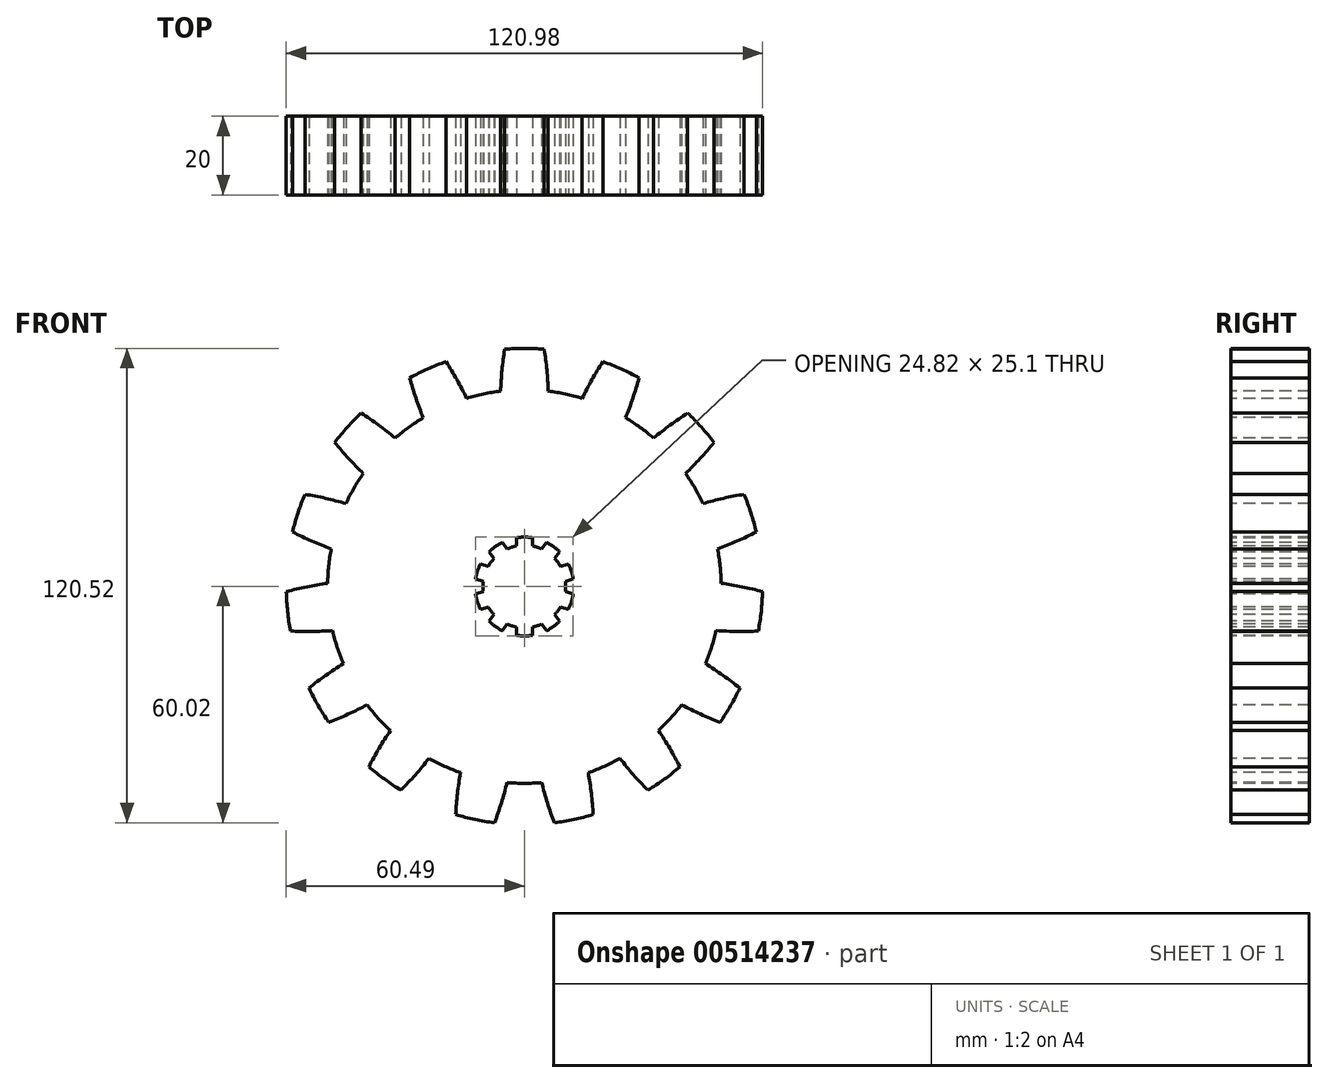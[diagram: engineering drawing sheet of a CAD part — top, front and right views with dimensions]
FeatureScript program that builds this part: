
annotation { "Feature Type Name" : "Feature", "Feature Type Description" : "" }
export const myFeature = defineFeature(function(context is Context, id is Id, definition is map)
    precondition{}
    {
        {
            var Q0;
            Q0=qCreatedBy(makeId("Front.planeOp"),FACE);
            var sketch = newSketch(context, id + "F0", { "sketchPlane" : qUnion([Q0])});
            skCircle(sketch, "E0", {"center": v(0, 0) * mm, "radius": 50 * mm});
            skArc(sketch, "E1", {"start": v(5.04, 60.29) * mm, "mid": v(0, 60.5) * mm, "end": v(-5.04, 60.29) * mm});
            skArc(sketch, "E2", {"start": v(-5.04, 60.29) * mm, "mid": v(-5.7, 54.98) * mm, "end": v(-6.05, 49.63) * mm});
            skArc(sketch, "E3.trimOffspring", {"start": v(6.05, 49.63) * mm, "mid": v(5.7, 54.98) * mm, "end": v(5.04, 60.29) * mm});
            skArc(sketch, "E4.1.0", {"start": v(-19.92, 57.13) * mm, "mid": v(-24.6, 55.27) * mm, "end": v(-29.12, 53.03) * mm});
            skArc(sketch, "E4.1.1", {"start": v(-14.66, 47.8) * mm, "mid": v(-17.15, 52.54) * mm, "end": v(-19.92, 57.13) * mm});
            skArc(sketch, "E4.1.2", {"start": v(-29.12, 53.03) * mm, "mid": v(-27.57, 47.9) * mm, "end": v(-25.71, 42.88) * mm});
            skArc(sketch, "E4.2.0", {"start": v(-41.43, 44.09) * mm, "mid": v(-44.96, 40.48) * mm, "end": v(-48.17, 36.6) * mm});
            skArc(sketch, "E4.2.1", {"start": v(-32.84, 37.7) * mm, "mid": v(-37.04, 41.02) * mm, "end": v(-41.43, 44.09) * mm});
            skArc(sketch, "E4.2.2", {"start": v(-48.17, 36.6) * mm, "mid": v(-44.67, 32.55) * mm, "end": v(-40.93, 28.72) * mm});
            skArc(sketch, "E5.3.3.0", {"start": v(-55.78, 23.42) * mm, "mid": v(-57.54, 18.7) * mm, "end": v(-58.9, 13.84) * mm});
            skArc(sketch, "E5.4.3.0", {"start": v(-45.34, 21.09) * mm, "mid": v(-50.52, 22.4) * mm, "end": v(-55.78, 23.42) * mm});
            skArc(sketch, "E5.8.3.0", {"start": v(-58.9, 13.84) * mm, "mid": v(-54.05, 11.57) * mm, "end": v(-49.07, 9.59) * mm});
            skArc(sketch, "E5.3.4.0", {"start": v(-60.49, -1.3) * mm, "mid": v(-60.17, -6.32) * mm, "end": v(-59.43, -11.31) * mm});
            skArc(sketch, "E5.4.4.0", {"start": v(-50, 0.82) * mm, "mid": v(-55.27, -0.08) * mm, "end": v(-60.49, -1.3) * mm});
            skArc(sketch, "E5.8.4.0", {"start": v(-59.43, -11.31) * mm, "mid": v(-54.08, -11.42) * mm, "end": v(-48.73, -11.2) * mm});
            skArc(sketch, "E5.3.5.0", {"start": v(-54.73, -25.78) * mm, "mid": v(-52.4, -30.25) * mm, "end": v(-49.7, -34.5) * mm});
            skArc(sketch, "E5.4.5.0", {"start": v(-46, -19.58) * mm, "mid": v(-50.46, -22.55) * mm, "end": v(-54.73, -25.78) * mm});
            skArc(sketch, "E5.8.5.0", {"start": v(-49.7, -34.5) * mm, "mid": v(-44.76, -32.42) * mm, "end": v(-39.96, -30.05) * mm});
            skArc(sketch, "E5.3.6.0", {"start": v(-39.51, -45.81) * mm, "mid": v(-35.56, -48.95) * mm, "end": v(-31.36, -51.74) * mm});
            skArc(sketch, "E5.4.6.0", {"start": v(-34.06, -36.6) * mm, "mid": v(-36.93, -41.13) * mm, "end": v(-39.51, -45.81) * mm});
            skArc(sketch, "E5.8.6.0", {"start": v(-31.36, -51.74) * mm, "mid": v(-27.7, -47.83) * mm, "end": v(-24.28, -43.7) * mm});
            skArc(sketch, "E5.3.7.0", {"start": v(-17.46, -57.93) * mm, "mid": v(-12.58, -59.18) * mm, "end": v(-7.6, -60.02) * mm});
            skArc(sketch, "E5.4.7.0", {"start": v(-16.23, -47.3) * mm, "mid": v(-17, -52.6) * mm, "end": v(-17.46, -57.93) * mm});
            skArc(sketch, "E5.8.7.0", {"start": v(-7.6, -60.02) * mm, "mid": v(-5.85, -54.96) * mm, "end": v(-4.4, -49.8) * mm});
            skArc(sketch, "E5.3.8.0", {"start": v(7.6, -60.02) * mm, "mid": v(12.58, -59.18) * mm, "end": v(17.46, -57.93) * mm});
            skArc(sketch, "E5.4.8.0", {"start": v(4.4, -49.8) * mm, "mid": v(5.85, -54.96) * mm, "end": v(7.6, -60.02) * mm});
            skArc(sketch, "E5.8.8.0", {"start": v(17.46, -57.93) * mm, "mid": v(17, -52.6) * mm, "end": v(16.23, -47.3) * mm});
            skArc(sketch, "E5.3.9.0", {"start": v(31.36, -51.74) * mm, "mid": v(35.56, -48.95) * mm, "end": v(39.51, -45.81) * mm});
            skArc(sketch, "E5.4.9.0", {"start": v(24.28, -43.7) * mm, "mid": v(27.7, -47.83) * mm, "end": v(31.36, -51.74) * mm});
            skArc(sketch, "E5.8.9.0", {"start": v(39.51, -45.81) * mm, "mid": v(36.93, -41.13) * mm, "end": v(34.06, -36.6) * mm});
            skArc(sketch, "E5.3.10.0", {"start": v(49.7, -34.5) * mm, "mid": v(52.4, -30.25) * mm, "end": v(54.73, -25.78) * mm});
            skArc(sketch, "E5.4.10.0", {"start": v(39.96, -30.05) * mm, "mid": v(44.76, -32.42) * mm, "end": v(49.7, -34.5) * mm});
            skArc(sketch, "E5.8.10.0", {"start": v(54.73, -25.78) * mm, "mid": v(50.46, -22.55) * mm, "end": v(46, -19.58) * mm});
            skArc(sketch, "E5.3.11.0", {"start": v(59.43, -11.31) * mm, "mid": v(60.17, -6.32) * mm, "end": v(60.49, -1.3) * mm});
            skArc(sketch, "E5.4.11.0", {"start": v(48.73, -11.2) * mm, "mid": v(54.08, -11.42) * mm, "end": v(59.43, -11.31) * mm});
            skArc(sketch, "E5.8.11.0", {"start": v(60.49, -1.3) * mm, "mid": v(55.27, -0.08) * mm, "end": v(50, 0.82) * mm});
            skArc(sketch, "E5.3.12.0", {"start": v(58.9, 13.84) * mm, "mid": v(57.54, 18.7) * mm, "end": v(55.78, 23.42) * mm});
            skArc(sketch, "E5.4.12.0", {"start": v(49.07, 9.59) * mm, "mid": v(54.05, 11.57) * mm, "end": v(58.9, 13.84) * mm});
            skArc(sketch, "E5.8.12.0", {"start": v(55.78, 23.42) * mm, "mid": v(50.52, 22.4) * mm, "end": v(45.34, 21.09) * mm});
            skArc(sketch, "E5.3.13.0", {"start": v(48.17, 36.6) * mm, "mid": v(44.96, 40.48) * mm, "end": v(41.43, 44.09) * mm});
            skArc(sketch, "E5.4.13.0", {"start": v(40.93, 28.72) * mm, "mid": v(44.67, 32.55) * mm, "end": v(48.17, 36.6) * mm});
            skArc(sketch, "E5.8.13.0", {"start": v(41.43, 44.09) * mm, "mid": v(37.04, 41.02) * mm, "end": v(32.84, 37.7) * mm});
            skArc(sketch, "E5.3.14.0", {"start": v(29.12, 53.03) * mm, "mid": v(24.6, 55.27) * mm, "end": v(19.92, 57.13) * mm});
            skArc(sketch, "E5.4.14.0", {"start": v(25.71, 42.88) * mm, "mid": v(27.57, 47.9) * mm, "end": v(29.12, 53.03) * mm});
            skArc(sketch, "E5.8.14.0", {"start": v(19.92, 57.13) * mm, "mid": v(17.15, 52.54) * mm, "end": v(14.66, 47.8) * mm});
            skSolve(sketch);
        }
        {
            var Q0;
            Q0 = qSketchRegion(id + "F0", true);
            extrude(context, id + "F1", {"entities" : qUnion([Q0]), "oppositeDirection" : true, "depth" : 20 * mm, "offsetDistance" : 25 * mm});
        }
        {
            var Q0;
            Q0=qCreatedBy(makeId("Front.planeOp"),FACE);
            var sketch = newSketch(context, id + "F2", { "sketchPlane" : qUnion([Q0])});
            skCircle(sketch, "E6", {"center": v(0, 0) * mm, "radius": 10.5 * mm});
            skArc(sketch, "E7", {"start": v(2.05, 12.38) * mm, "mid": v(0, 12.55) * mm, "end": v(-2.05, 12.38) * mm});
            skLineSegment(sketch, "E8", {"start": v(-2.05, 12.38) * mm, "end": v(-2.05, 10.3) * mm});
            skLineSegment(sketch, "E9", {"start": v(2.05, 12.38) * mm, "end": v(2.05, 10.3) * mm});
            skArc(sketch, "E10.1.0", {"start": v(-5.62, 11.22) * mm, "mid": v(-7.38, 10.15) * mm, "end": v(-8.94, 8.81) * mm});
            skLineSegment(sketch, "E10.1.1", {"start": v(-8.94, 8.81) * mm, "end": v(-7.71, 7.13) * mm});
            skLineSegment(sketch, "E10.1.2", {"start": v(-5.62, 11.22) * mm, "end": v(-4.4, 9.54) * mm});
            skArc(sketch, "E10.2.0", {"start": v(-11.14, 5.78) * mm, "mid": v(-11.94, 3.88) * mm, "end": v(-12.4, 1.88) * mm});
            skLineSegment(sketch, "E10.2.1", {"start": v(-12.4, 1.88) * mm, "end": v(-10.43, 1.23) * mm});
            skLineSegment(sketch, "E10.2.2", {"start": v(-11.14, 5.78) * mm, "end": v(-9.16, 5.13) * mm});
            skArc(sketch, "E11.3.3.0", {"start": v(-12.4, -1.88) * mm, "mid": v(-11.94, -3.88) * mm, "end": v(-11.14, -5.78) * mm});
            skLineSegment(sketch, "E11.4.3.0", {"start": v(-11.14, -5.78) * mm, "end": v(-9.16, -5.13) * mm});
            skLineSegment(sketch, "E11.7.3.0", {"start": v(-12.4, -1.88) * mm, "end": v(-10.43, -1.23) * mm});
            skArc(sketch, "E11.3.4.0", {"start": v(-8.94, -8.81) * mm, "mid": v(-7.38, -10.15) * mm, "end": v(-5.62, -11.22) * mm});
            skLineSegment(sketch, "E11.4.4.0", {"start": v(-5.62, -11.22) * mm, "end": v(-4.4, -9.54) * mm});
            skLineSegment(sketch, "E11.7.4.0", {"start": v(-8.94, -8.81) * mm, "end": v(-7.71, -7.13) * mm});
            skArc(sketch, "E11.3.5.0", {"start": v(-2.05, -12.38) * mm, "mid": v(0, -12.55) * mm, "end": v(2.05, -12.38) * mm});
            skLineSegment(sketch, "E11.4.5.0", {"start": v(2.05, -12.38) * mm, "end": v(2.05, -10.3) * mm});
            skLineSegment(sketch, "E11.7.5.0", {"start": v(-2.05, -12.38) * mm, "end": v(-2.05, -10.3) * mm});
            skArc(sketch, "E11.3.6.0", {"start": v(5.62, -11.22) * mm, "mid": v(7.38, -10.15) * mm, "end": v(8.94, -8.81) * mm});
            skLineSegment(sketch, "E11.4.6.0", {"start": v(8.94, -8.81) * mm, "end": v(7.71, -7.13) * mm});
            skLineSegment(sketch, "E11.7.6.0", {"start": v(5.62, -11.22) * mm, "end": v(4.4, -9.54) * mm});
            skArc(sketch, "E11.3.7.0", {"start": v(11.14, -5.78) * mm, "mid": v(11.94, -3.88) * mm, "end": v(12.4, -1.88) * mm});
            skLineSegment(sketch, "E11.4.7.0", {"start": v(12.4, -1.88) * mm, "end": v(10.43, -1.23) * mm});
            skLineSegment(sketch, "E11.7.7.0", {"start": v(11.14, -5.78) * mm, "end": v(9.16, -5.13) * mm});
            skArc(sketch, "E11.3.8.0", {"start": v(12.4, 1.88) * mm, "mid": v(11.94, 3.88) * mm, "end": v(11.14, 5.78) * mm});
            skLineSegment(sketch, "E11.4.8.0", {"start": v(11.14, 5.78) * mm, "end": v(9.16, 5.13) * mm});
            skLineSegment(sketch, "E11.7.8.0", {"start": v(12.4, 1.88) * mm, "end": v(10.43, 1.23) * mm});
            skArc(sketch, "E11.3.9.0", {"start": v(8.94, 8.81) * mm, "mid": v(7.38, 10.15) * mm, "end": v(5.62, 11.22) * mm});
            skLineSegment(sketch, "E11.4.9.0", {"start": v(5.62, 11.22) * mm, "end": v(4.4, 9.54) * mm});
            skLineSegment(sketch, "E11.7.9.0", {"start": v(8.94, 8.81) * mm, "end": v(7.71, 7.13) * mm});
            skSolve(sketch);
        }
        {
            var Q0;
            Q0 = qSketchRegion(id + "F2", true);
            extrude(context, id + "F3", {"entities" : qUnion([Q0]), "operationType" : NewBodyOperationType.REMOVE, "oppositeDirection" : true, "depth" : 20 * mm, "offsetDistance" : 25 * mm});
        }
    });
